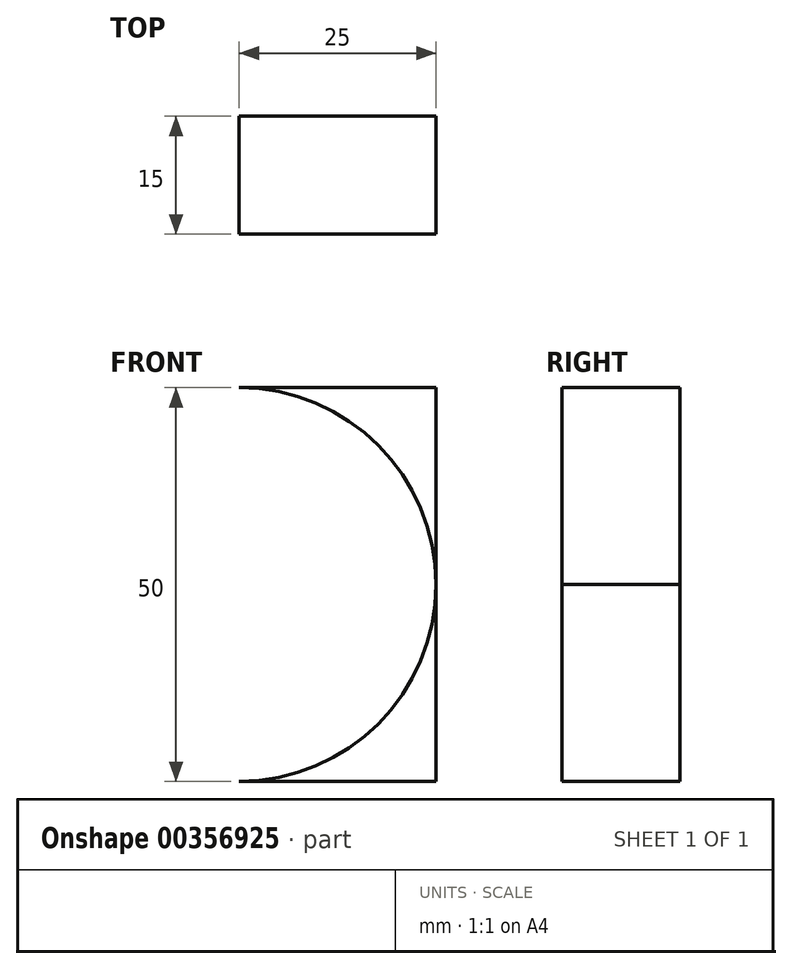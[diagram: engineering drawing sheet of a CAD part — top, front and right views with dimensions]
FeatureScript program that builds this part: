
annotation { "Feature Type Name" : "Feature", "Feature Type Description" : "" }
export const myFeature = defineFeature(function(context is Context, id is Id, definition is map)
    precondition{}
    {
        {
            var Q0;
            Q0=qCreatedBy(makeId("Front.planeOp"),FACE);
            var sketch = newSketch(context, id + "F0", { "sketchPlane" : qUnion([Q0])});
            skLineSegment(sketch, "E0.bottom", {"start": v(70, 25) * mm, "end": v(-70, 25) * mm});
            skLineSegment(sketch, "E0.top", {"start": v(70, -25) * mm, "end": v(-70, -25) * mm});
            skLineSegment(sketch, "E0.left", {"start": v(70, 25) * mm, "end": v(70, -25) * mm});
            skLineSegment(sketch, "E0.right", {"start": v(-70, 25) * mm, "end": v(-70, -25) * mm});
            skPoint(sketch, "E0.middle", {"position": v(0, 0) * mm});
            skPoint(sketch, "E1", {"position": v(-45, 0) * mm});
            skPoint(sketch, "E2", {"position": v(45, 0) * mm});
            skCircle(sketch, "E3", {"center": v(-45, 0) * mm, "radius": 10 * mm});
            skCircle(sketch, "E4", {"center": v(-45, 0) * mm, "radius": 24.96 * mm});
            skCircle(sketch, "E5", {"center": v(45, 0) * mm, "radius": 10 * mm});
            skCircle(sketch, "E6", {"center": v(45, 0) * mm, "radius": 25 * mm});
            skSolve(sketch);
        }
        {
            var Q0;
            {var subQ0=sQuery(id+"F0.wireOp",EDGE,"E0.left");var subQ1=sQuery(id+"F0.wireOp",EDGE,"E0.bottom");var subQ2=makeQuery(id+"F0.imprint","INTERSECT",VERTEX,{"derivedFrom":[subQ1,subQ0]});Q0=makeQuery(id+"F0.imprint","IMPRINT",FACE,{"disambiguationData":[TD([[makeQuery(id+"F0.imprint","IMPRINT",EDGE,{"disambiguationData":[TD([[subQ2,-1.0]])],"derivedFrom":subQ1}),1.0]])]});}
            var Q1;
            {var subQ0=sQuery(id+"F0.wireOp",EDGE,"E0.left");var subQ1=sQuery(id+"F0.wireOp",EDGE,"E0.top");var subQ2=makeQuery(id+"F0.imprint","INTERSECT",VERTEX,{"derivedFrom":[subQ1,subQ0]});Q1=makeQuery(id+"F0.imprint","IMPRINT",FACE,{"disambiguationData":[TD([[makeQuery(id+"F0.imprint","IMPRINT",EDGE,{"disambiguationData":[TD([[subQ2,-1.0]])],"derivedFrom":subQ1}),-1.0]])]});}
            extrude(context, id + "F1", {"entities" : qUnion([Q0, Q1]), "depth" : 15 * mm});
        }
    });
